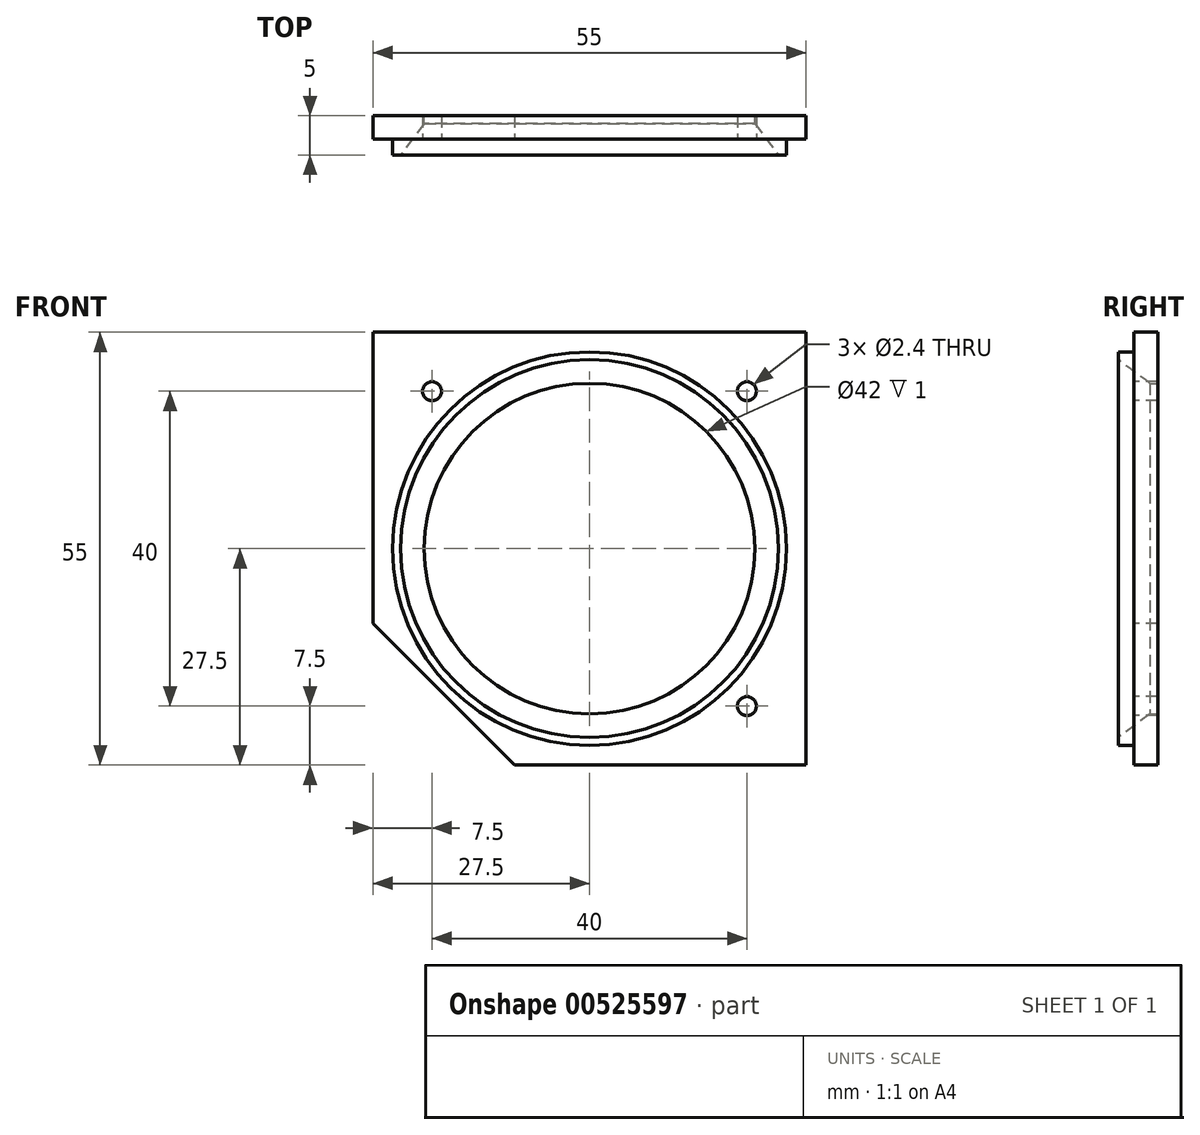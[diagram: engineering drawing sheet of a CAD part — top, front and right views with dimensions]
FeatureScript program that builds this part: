
annotation { "Feature Type Name" : "Feature", "Feature Type Description" : "" }
export const myFeature = defineFeature(function(context is Context, id is Id, definition is map)
    precondition{}
    {
        {
            var Q0;
            Q0=qCreatedBy(makeId("Right.planeOp"),FACE);
            var sketch = newSketch(context, id + "F0", { "sketchPlane" : qUnion([Q0])});
            skLineSegment(sketch, "E0", {"start": v(19.32, 0) * mm, "end": v(-16.11, 0) * mm, "construction": true});
            skLineSegment(sketch, "E1", {"start": v(-3, 25) * mm, "end": v(-3, 24) * mm});
            skLineSegment(sketch, "E2", {"start": v(2, 21) * mm, "end": v(2, 25) * mm});
            skLineSegment(sketch, "E3", {"start": v(2, 25) * mm, "end": v(-3, 25) * mm});
            skLineSegment(sketch, "E4", {"start": v(2, 21) * mm, "end": v(1, 21) * mm});
            skLineSegment(sketch, "E5", {"start": v(1, 21) * mm, "end": v(-3, 24) * mm});
            skSolve(sketch);
        }
        {
            var Q0;
            Q0=qSketchRegion(id+"F0",true);
            var Q1;
            Q1=sQuery(id+"F0.wireOp",EDGE,"E0");
            revolve(context, id + "F1", {"entities" : qUnion([Q0]), "axis" : qUnion([Q1]), "revolveType" : RevolveType.FULL});
        }
        {
            var Q0;
            Q0=makeQuery(id+"F1.opRevolve","SWEPT_FACE",FACE,{"disambiguationData":[OSD([sQuery(id+"F0.wireOp",EDGE,"E1")])]});
            cPlane(context, id + "F2", {"entities" : qUnion([Q0]), "cplaneType" : CPlaneType.OFFSET, "offset" : 2 * mm, "oppositeDirection" : true, "width" : 150 * mm, "height" : 150 * mm});
        }
        {
            var Q0;
            Q0=qCreatedBy(id+"F2.planeOp",FACE);
            var sketch = newSketch(context, id + "F3", { "sketchPlane" : qUnion([Q0])});
            skPoint(sketch, "E6.middle", {"position": v(0, 0) * mm});
            skCircle(sketch, "E7", {"center": v(-20, 20) * mm, "radius": 1.2 * mm});
            skCircle(sketch, "E8", {"center": v(20, -20) * mm, "radius": 1.2 * mm});
            skCircle(sketch, "E9", {"center": v(20, 20) * mm, "radius": 1.2 * mm});
            skLineSegment(sketch, "E10.bottom", {"start": v(27.5, -27.5) * mm, "end": v(-9.5, -27.5) * mm});
            skLineSegment(sketch, "E10.top", {"start": v(27.5, 27.5) * mm, "end": v(-27.5, 27.5) * mm});
            skLineSegment(sketch, "E10.left", {"start": v(27.5, -27.5) * mm, "end": v(27.5, 27.5) * mm});
            skLineSegment(sketch, "E10.right", {"start": v(-27.5, -9.5) * mm, "end": v(-27.5, 27.5) * mm});
            skLineSegment(sketch, "E11", {"start": v(-9.5, -27.5) * mm, "end": v(-27.5, -9.5) * mm});
            skCircle(sketch, "E12", {"center": v(0, 0) * mm, "radius": 25 * mm});
            skSolve(sketch);
        }
        {
            var Q0;
            Q0=qSketchRegion(id+"F3",true);
            extrude(context, id + "F4", {"entities" : qUnion([Q0]), "operationType" : NewBodyOperationType.ADD, "oppositeDirection" : true, "depth" : 3 * mm, "offsetDistance" : 25 * mm});
        }
    });
